# Revit family: xSoap_Dispenser-Sloan-ESD-800
name_source: partatom
category: Specialty Equipment
revit_build: Autodesk Revit 2014 (Build: 20130308_1515(x64)
units: mm (PartAtom-declared; Revit-internal decimal feet)

## types (1)
- ESD-800
    ADA Compliant = Yes
    Assembly Code = E1010900
    Code Number = 3346097
    Countertop Thickness = 1"
    Default Elevation = 0"
    Description = Sensor Activated Electonic Soap Dispenser
    Finish = Die Cast-Sloan-Chrome Plated
    Height = 4 1/4"
    Installation Type = Deck Mounted
    Length = 4 1/2"
    Manufacturer = SLOAN
    Material = Die Cast-Sloan-Chrome Plated
    Model = ESD-800
    Operation = Sensor Activated
    Price = Prices may vary. Please consult Manufacturer Representative for most up-to-date price list.
    Product Documentation Link = https://specifications.sloan.com
    Product Page URL = https://www.sloan.com
    URL = https://www.sloan.com
    Voltage = 120 V
    Warranty Information = 3 Year Limited Warranty
    Width = 2"

## geometry (parser evidence)
native form markers: Sweep x1
no freeform markers — native parametric forms only
